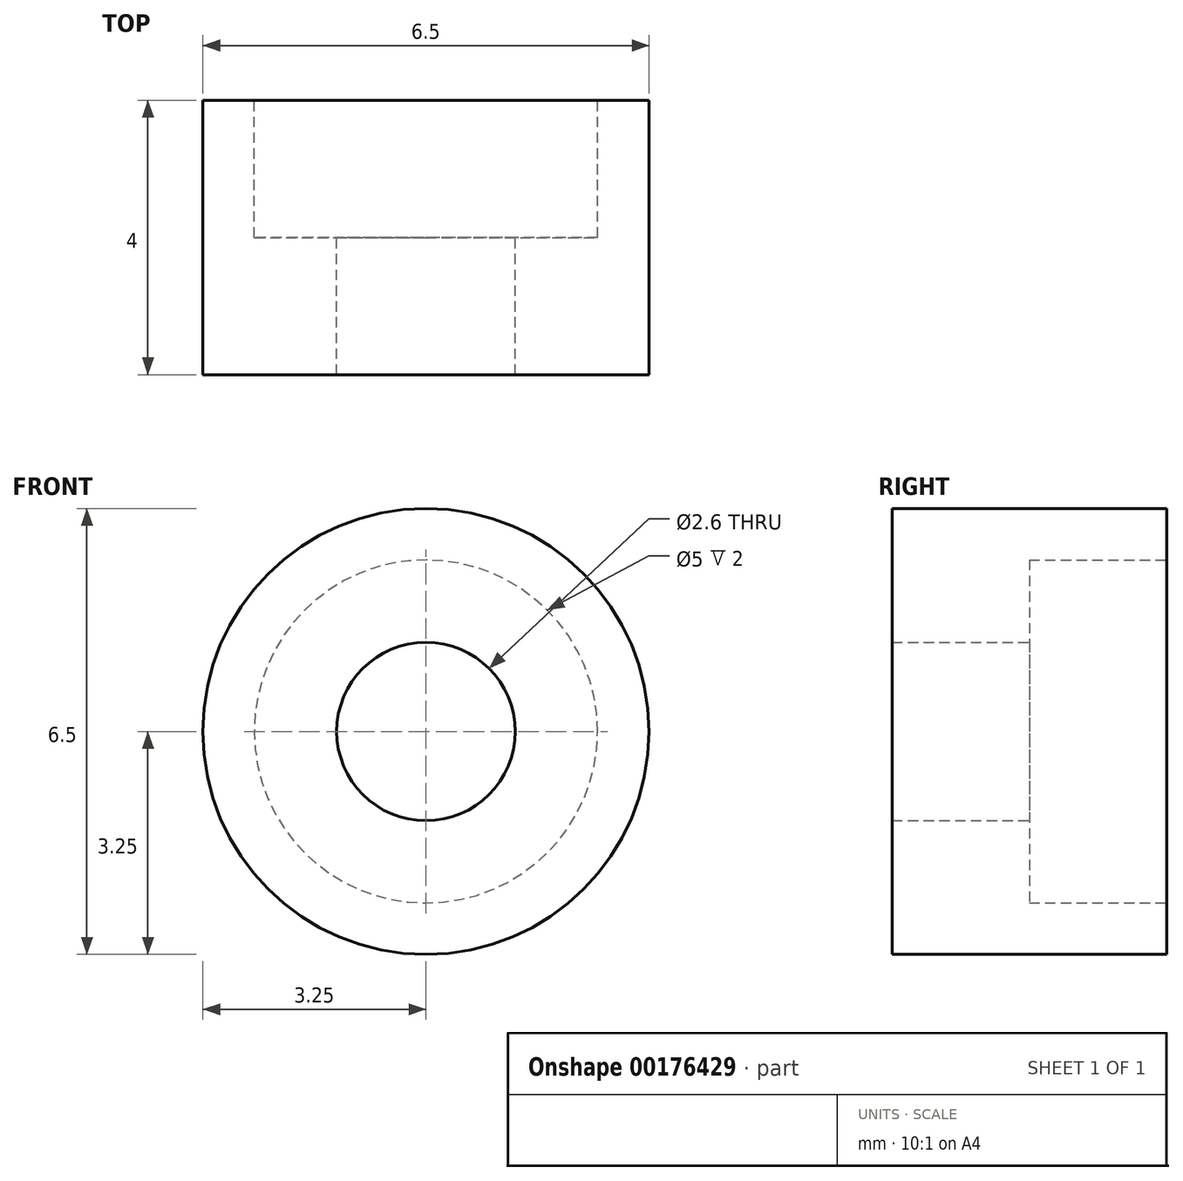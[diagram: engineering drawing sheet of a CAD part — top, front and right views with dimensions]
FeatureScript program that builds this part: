
annotation { "Feature Type Name" : "Feature", "Feature Type Description" : "" }
export const myFeature = defineFeature(function(context is Context, id is Id, definition is map)
    precondition{}
    {
        {
            var Q0;
            Q0=qCreatedBy(makeId("Right.planeOp"),FACE);
            var sketch = newSketch(context, id + "F0", { "sketchPlane" : qUnion([Q0])});
            skLineSegment(sketch, "E0", {"start": v(11.47, 0) * mm, "end": v(0, 0) * mm, "construction": true});
            skLineSegment(sketch, "E1", {"start": v(2, 1.3) * mm, "end": v(0, 1.3) * mm});
            skLineSegment(sketch, "E2", {"start": v(2, 1.3) * mm, "end": v(2, 2.5) * mm});
            skLineSegment(sketch, "E3", {"start": v(4, 2.5) * mm, "end": v(2, 2.5) * mm});
            skLineSegment(sketch, "E4", {"start": v(4, 2.5) * mm, "end": v(4, 3.25) * mm});
            skLineSegment(sketch, "E5", {"start": v(2, 3.25) * mm, "end": v(4, 3.25) * mm});
            skLineSegment(sketch, "E6", {"start": v(2, 3.25) * mm, "end": v(2, 3.25) * mm});
            skLineSegment(sketch, "E7", {"start": v(0, 3.25) * mm, "end": v(2, 3.25) * mm});
            skLineSegment(sketch, "E8", {"start": v(0, 3.25) * mm, "end": v(0, 1.3) * mm});
            skSolve(sketch);
        }
        {
            var Q0;
            Q0=makeQuery(id+"F0.imprint","IMPRINT",FACE,{"disambiguationData":[TD([[makeQuery(id+"F0.imprint","IMPRINT",EDGE,{"derivedFrom":sQuery(id+"F0.wireOp",EDGE,"E1")}),-1.0]])]});
            var Q1;
            Q1=sQuery(id+"F0.wireOp",EDGE,"E0");
            revolve(context, id + "F1", {"entities" : qUnion([Q0]), "axis" : qUnion([Q1]), "revolveType" : RevolveType.FULL});
        }
    });
